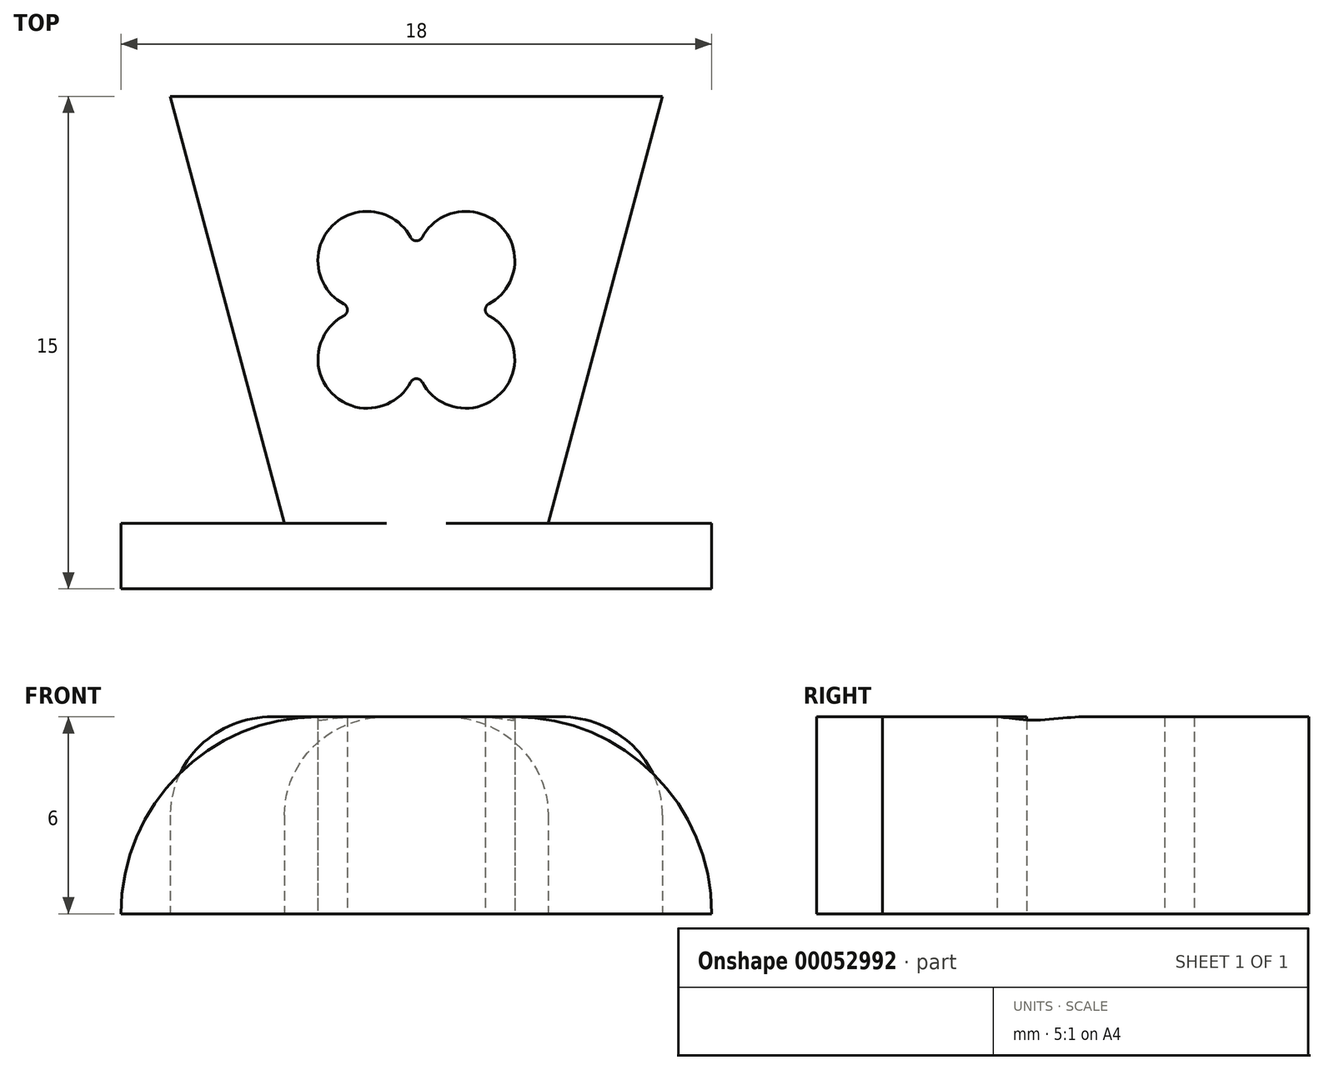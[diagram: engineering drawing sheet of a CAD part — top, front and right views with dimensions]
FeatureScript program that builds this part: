
annotation { "Feature Type Name" : "Feature", "Feature Type Description" : "" }
export const myFeature = defineFeature(function(context is Context, id is Id, definition is map)
    precondition{}
    {
        {
            var Q0;
            Q0=qCreatedBy(makeId("Top.planeOp"),FACE);
            var sketch = newSketch(context, id + "F0", { "sketchPlane" : qUnion([Q0])});
            skLineSegment(sketch, "E0.bottom", {"start": v(-9, -7) * mm, "end": v(9, -7) * mm});
            skLineSegment(sketch, "E0.left", {"start": v(-9, -7) * mm, "end": v(-9, -5) * mm});
            skLineSegment(sketch, "E0.right", {"start": v(9, -7) * mm, "end": v(9, -5) * mm});
            skLineSegment(sketch, "E1.top", {"start": v(7.5, 8) * mm, "end": v(-7.5, 8) * mm});
            skLineSegment(sketch, "E2", {"start": v(-9, -5) * mm, "end": v(9, -5) * mm});
            skLineSegment(sketch, "E3", {"start": v(-7.5, 8) * mm, "end": v(-4.02, -5) * mm});
            skLineSegment(sketch, "E4", {"start": v(0, 8) * mm, "end": v(0, -5) * mm, "construction": true});
            skLineSegment(sketch, "E5.MirrorCS", {"start": v(7.5, 8) * mm, "end": v(4.02, -5) * mm});
            skLineSegment(sketch, "E6.0", {"start": v(1.5, 0) * mm, "end": v(-1.5, 0) * mm, "construction": true});
            skLineSegment(sketch, "E6.1", {"start": v(-1.5, 0) * mm, "end": v(-1.5, 3) * mm, "construction": true});
            skLineSegment(sketch, "E6.2", {"start": v(-1.5, 3) * mm, "end": v(1.5, 3) * mm, "construction": true});
            skLineSegment(sketch, "E6.3", {"start": v(1.5, 3) * mm, "end": v(1.5, 0) * mm, "construction": true});
            skPoint(sketch, "E6.0.midPoint", {"position": v(0, 0) * mm});
            skArc(sketch, "E7", {"start": v(0, 3) * mm, "mid": v(-2.56, 4.06) * mm, "end": v(-1.5, 1.5) * mm});
            skArc(sketch, "E8", {"start": v(1.5, 1.5) * mm, "mid": v(2.56, 4.06) * mm, "end": v(0, 3) * mm});
            skArc(sketch, "E9", {"start": v(0, 0) * mm, "mid": v(2.56, -1.06) * mm, "end": v(1.5, 1.5) * mm});
            skArc(sketch, "E10", {"start": v(-1.5, 1.5) * mm, "mid": v(-2.56, -1.06) * mm, "end": v(0, 0) * mm});
            skLineSegment(sketch, "E11", {"start": v(-4.42, -3.5) * mm, "end": v(4.42, -3.5) * mm});
            skSolve(sketch);
        }
        {
            var Q0;
            {var subQ1=sQuery(id+"F0.wireOp",EDGE,"E1.top");Q0=makeQuery(id+"F0.imprint","IMPRINT",FACE,{"disambiguationData":[TD([[makeQuery(id+"F0.imprint","IMPRINT",EDGE,{"derivedFrom":subQ1}),1.0]])]});}
            var Q1;
            Q1=makeQuery(id+"F0.imprint","IMPRINT",FACE,{"disambiguationData":[TD([[makeQuery(id+"F0.imprint","IMPRINT",EDGE,{"derivedFrom":sQuery(id+"F0.wireOp",EDGE,"E0.bottom")}),1.0]])]});
            var Q2;
            {var subQ5=sQuery(id+"F0.wireOp",EDGE,"E11");Q2=makeQuery(id+"F0.imprint","IMPRINT",FACE,{"disambiguationData":[TD([[makeQuery(id+"F0.imprint","IMPRINT",EDGE,{"derivedFrom":subQ5}),-1.0]])]});}
            extrude(context, id + "F1", {"entities" : qUnion([Q0, Q1, Q2]), "depth" : 6 * mm});
        }
        {
            var Q0;
            Q0=makeQuery(id+"F1.opExtrude","SWEPT_EDGE",EDGE,{"disambiguationData":[OSD([sQuery(id+"F0.wireOp",EDGE,"E7"),sQuery(id+"F0.wireOp",EDGE,"E10")])]});
            var Q1;
            Q1=makeQuery(id+"F1.opExtrude","SWEPT_EDGE",EDGE,{"disambiguationData":[OSD([sQuery(id+"F0.wireOp",EDGE,"E7"),sQuery(id+"F0.wireOp",EDGE,"E8")])]});
            var Q2;
            Q2=makeQuery(id+"F1.opExtrude","SWEPT_EDGE",EDGE,{"disambiguationData":[OSD([sQuery(id+"F0.wireOp",EDGE,"E8"),sQuery(id+"F0.wireOp",EDGE,"E9")])]});
            var Q3;
            Q3=makeQuery(id+"F1.opExtrude","SWEPT_EDGE",EDGE,{"disambiguationData":[OSD([sQuery(id+"F0.wireOp",EDGE,"E9"),sQuery(id+"F0.wireOp",EDGE,"E10")])]});
            fillet(context, id + "F2", {"entities" : qUnion([Q0, Q1, Q2, Q3]), "radius" : 0.2 * mm, "tangentPropagation" : true, "allowEdgeOverflow" : false});
        }
        {
            var Q0;
            Q0=makeQuery(id+"F1.opExtrude","CAP_EDGE",EDGE,{"disambiguationData":[OSD([sQuery(id+"F0.wireOp",EDGE,"E3")])],"isStart":false});
            var Q1;
            Q1=makeQuery(id+"F1.opExtrude","CAP_EDGE",EDGE,{"disambiguationData":[OSD([sQuery(id+"F0.wireOp",EDGE,"E5.MirrorCS")])],"isStart":false});
            fillet(context, id + "F3", {"entities" : qUnion([Q0, Q1]), "radius" : 3 * mm, "tangentPropagation" : true, "allowEdgeOverflow" : false});
        }
        {
            var Q0;
            Q0=makeQuery(id+"F1.opExtrude","CAP_EDGE",EDGE,{"disambiguationData":[OSD([sQuery(id+"F0.wireOp",EDGE,"E0.right")])],"isStart":false});
            var Q1;
            Q1=makeQuery(id+"F1.opExtrude","CAP_EDGE",EDGE,{"disambiguationData":[OSD([sQuery(id+"F0.wireOp",EDGE,"E0.left")])],"isStart":false});
            fillet(context, id + "F4", {"entities" : qUnion([Q0, Q1]), "radius" : 6 * mm, "tangentPropagation" : true, "allowEdgeOverflow" : false});
        }
    });
